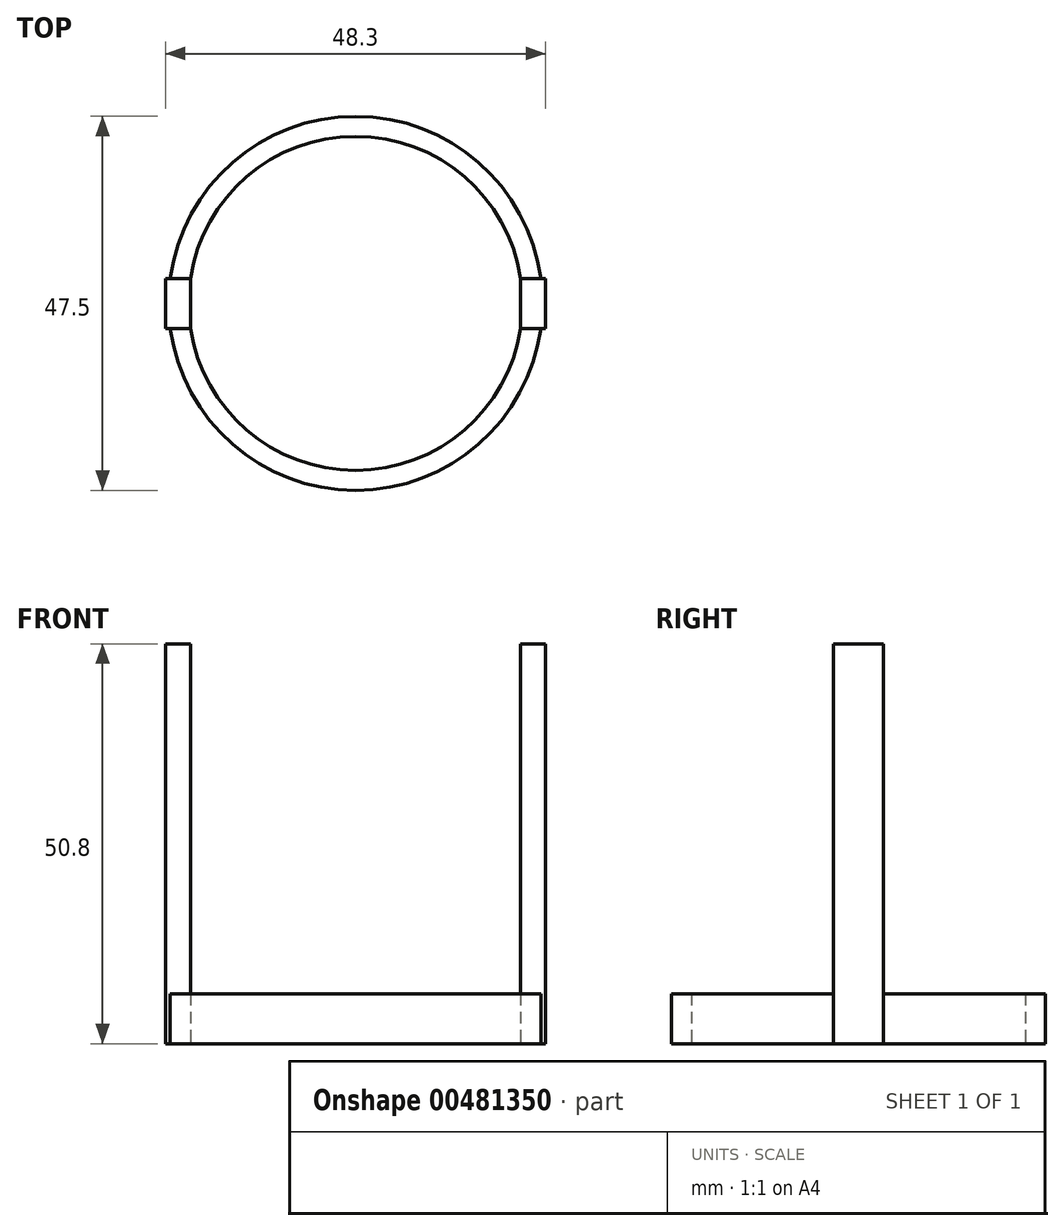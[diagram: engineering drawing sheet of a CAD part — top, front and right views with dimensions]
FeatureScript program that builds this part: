
annotation { "Feature Type Name" : "Feature", "Feature Type Description" : "" }
export const myFeature = defineFeature(function(context is Context, id is Id, definition is map)
    precondition{}
    {
        {
            var Q0;
            Q0=qCreatedBy(makeId("Top.planeOp"),FACE);
            var sketch = newSketch(context, id + "F0", { "sketchPlane" : qUnion([Q0])});
            skArc(sketch, "E0", {"start": v(-20.97, -3.18) * mm, "mid": v(0, -21.2) * mm, "end": v(20.97, -3.17) * mm});
            skArc(sketch, "E1", {"start": v(-23.54, -3.17) * mm, "mid": v(0, -23.75) * mm, "end": v(23.54, -3.17) * mm});
            skLineSegment(sketch, "E2.bottom", {"start": v(-24.15, 3.18) * mm, "end": v(-20.97, 3.18) * mm});
            skLineSegment(sketch, "E2.top", {"start": v(-24.15, -3.18) * mm, "end": v(-20.97, -3.18) * mm});
            skLineSegment(sketch, "E2.left", {"start": v(-24.15, 3.18) * mm, "end": v(-24.15, -3.18) * mm});
            skLineSegment(sketch, "E2.right", {"start": v(-20.97, 3.17) * mm, "end": v(-20.97, -3.18) * mm});
            skPoint(sketch, "E2.middle", {"position": v(-22.56, 0) * mm});
            skLineSegment(sketch, "E3.bottom", {"start": v(24.15, -3.17) * mm, "end": v(20.97, -3.17) * mm});
            skLineSegment(sketch, "E3.top", {"start": v(24.15, 3.18) * mm, "end": v(20.97, 3.18) * mm});
            skLineSegment(sketch, "E3.left", {"start": v(24.15, -3.17) * mm, "end": v(24.15, 3.18) * mm});
            skLineSegment(sketch, "E3.right", {"start": v(20.97, -3.17) * mm, "end": v(20.97, 3.18) * mm});
            skPoint(sketch, "E3.middle", {"position": v(22.56, 0) * mm});
            skArc(sketch, "E4.trimOffspring", {"start": v(20.97, 3.17) * mm, "mid": v(0, 21.2) * mm, "end": v(-20.97, 3.17) * mm});
            skArc(sketch, "E5.trimOffspring", {"start": v(23.54, 3.18) * mm, "mid": v(0, 23.75) * mm, "end": v(-23.54, 3.17) * mm});
            skSolve(sketch);
        }
        {
            var Q0;
            {var subQ3=sQuery(id+"F0.wireOp",EDGE,"E2.left");Q0=makeQuery(id+"F0.imprint","IMPRINT",FACE,{"disambiguationData":[TD([[makeQuery(id+"F0.imprint","IMPRINT",EDGE,{"derivedFrom":subQ3}),1.0]])]});}
            var Q1;
            {var subQ3=sQuery(id+"F0.wireOp",EDGE,"E3.left");Q1=makeQuery(id+"F0.imprint","IMPRINT",FACE,{"disambiguationData":[TD([[makeQuery(id+"F0.imprint","IMPRINT",EDGE,{"derivedFrom":subQ3}),1.0]])]});}
            extrude(context, id + "F1", {"entities" : qUnion([Q0, Q1]), "depth" : 50.8 * mm});
        }
        {
            var Q0;
            Q0 = qSketchRegion(id + "F0", true);
            extrude(context, id + "F2", {"entities" : qUnion([Q0]), "operationType" : NewBodyOperationType.ADD, "depth" : 6.35 * mm});
        }
    });
